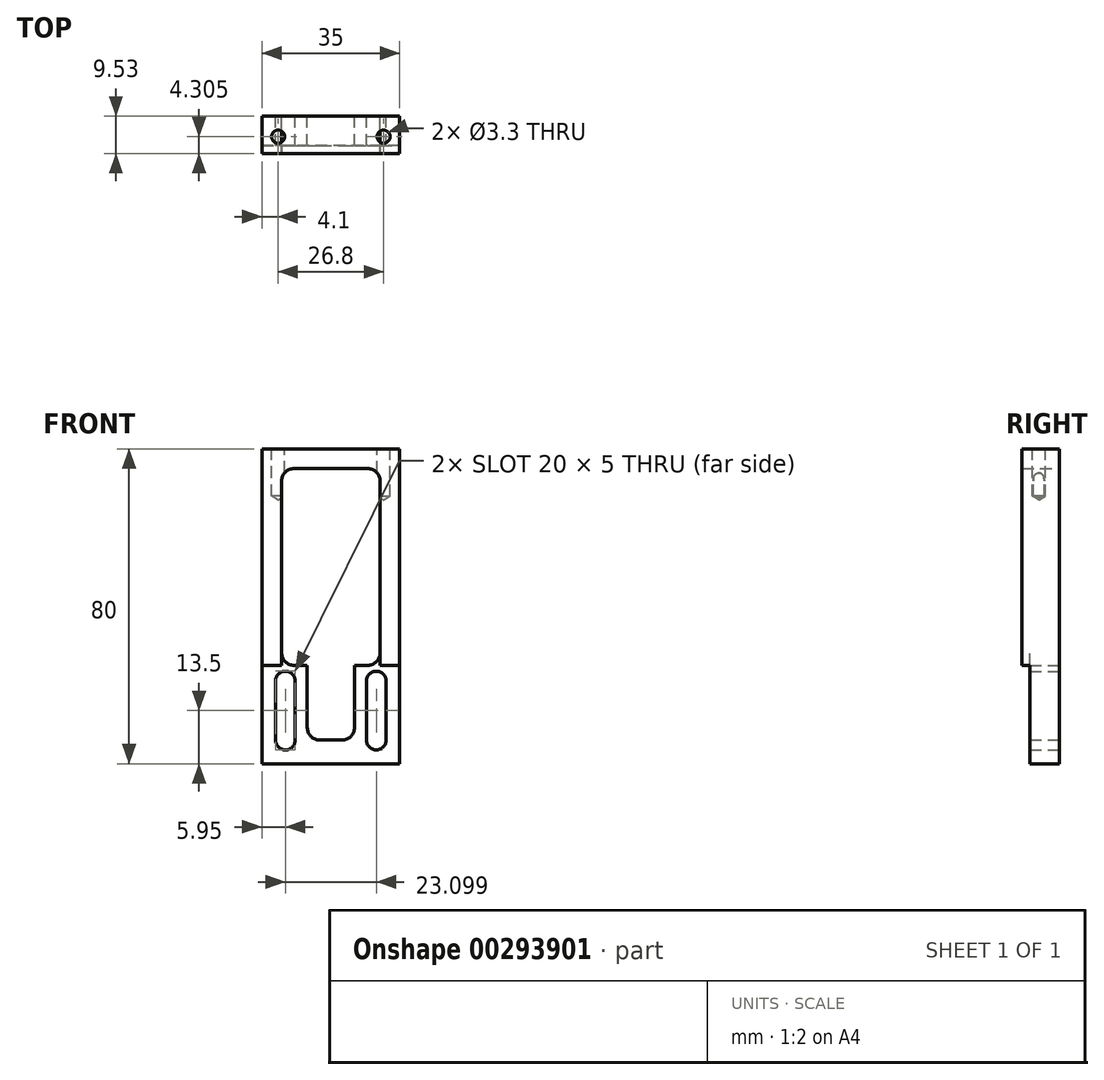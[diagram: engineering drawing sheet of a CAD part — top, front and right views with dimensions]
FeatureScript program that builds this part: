
annotation { "Feature Type Name" : "Feature", "Feature Type Description" : "" }
export const myFeature = defineFeature(function(context is Context, id is Id, definition is map)
    precondition{}
    {
        {
            var Q0;
            Q0=qCreatedBy(makeId("Front.planeOp"),FACE);
            var sketch = newSketch(context, id + "F0", { "sketchPlane" : qUnion([Q0])});
            skLineSegment(sketch, "E0.bottom", {"start": v(17.5, -40) * mm, "end": v(-17.5, -40) * mm});
            skLineSegment(sketch, "E0.top", {"start": v(17.5, 40) * mm, "end": v(-17.5, 40) * mm});
            skLineSegment(sketch, "E0.left", {"start": v(17.5, -40) * mm, "end": v(17.5, 40) * mm});
            skLineSegment(sketch, "E0.right", {"start": v(-17.5, -40) * mm, "end": v(-17.5, 40) * mm});
            skPoint(sketch, "E0.middle", {"position": v(0, 0) * mm});
            skLineSegment(sketch, "E1", {"start": v(-17.5, -15) * mm, "end": v(17.5, -15) * mm});
            skLineSegment(sketch, "E2.bottom", {"start": v(-9.33, 35) * mm, "end": v(9.32, 35) * mm});
            skLineSegment(sketch, "E2.top", {"start": v(-9.32, -15) * mm, "end": v(9.32, -15) * mm});
            skLineSegment(sketch, "E2.left", {"start": v(-12.5, 31.83) * mm, "end": v(-12.5, -11.82) * mm});
            skLineSegment(sketch, "E2.right", {"start": v(12.5, 31.83) * mm, "end": v(12.5, -11.82) * mm});
            skLineSegment(sketch, "E3.bottom", {"start": v(-6, -15) * mm, "end": v(6, -15) * mm});
            skLineSegment(sketch, "E3.top", {"start": v(-2.82, -34) * mm, "end": v(2.83, -34) * mm});
            skLineSegment(sketch, "E3.left", {"start": v(-6, -15) * mm, "end": v(-6, -30.83) * mm});
            skLineSegment(sketch, "E3.right", {"start": v(6, -15) * mm, "end": v(6, -30.83) * mm});
            skPoint(sketch, "E4.visualSharp", {"position": v(-12.5, 35) * mm});
            skArc(sketch, "E4.filletArc", {"start": v(-9.33, 35) * mm, "mid": v(-11.57, 34.07) * mm, "end": v(-12.5, 31.83) * mm});
            skPoint(sketch, "E5.visualSharp", {"position": v(12.5, 35) * mm});
            skArc(sketch, "E5.filletArc", {"start": v(12.5, 31.83) * mm, "mid": v(11.57, 34.07) * mm, "end": v(9.32, 35) * mm});
            skPoint(sketch, "E6.visualSharp", {"position": v(-12.5, -15) * mm});
            skArc(sketch, "E6.filletArc", {"start": v(-12.5, -11.82) * mm, "mid": v(-11.57, -14.07) * mm, "end": v(-9.32, -15) * mm});
            skPoint(sketch, "E7.visualSharp", {"position": v(12.5, -15) * mm});
            skArc(sketch, "E7.filletArc", {"start": v(9.32, -15) * mm, "mid": v(11.57, -14.07) * mm, "end": v(12.5, -11.82) * mm});
            skPoint(sketch, "E8.visualSharp", {"position": v(-6, -34) * mm});
            skArc(sketch, "E8.filletArc", {"start": v(-6, -30.83) * mm, "mid": v(-5.07, -33.07) * mm, "end": v(-2.82, -34) * mm});
            skPoint(sketch, "E9.visualSharp", {"position": v(6, -34) * mm});
            skArc(sketch, "E9.filletArc", {"start": v(2.83, -34) * mm, "mid": v(5.07, -33.07) * mm, "end": v(6, -30.83) * mm});
            skLineSegment(sketch, "E10.bottom", {"start": v(-11.55, -36.5) * mm, "end": v(-11.55, -36.5) * mm});
            skLineSegment(sketch, "E10.top", {"start": v(-11.55, -16.5) * mm, "end": v(-11.55, -16.5) * mm});
            skLineSegment(sketch, "E10.left", {"start": v(-9.05, -34) * mm, "end": v(-9.05, -19) * mm});
            skLineSegment(sketch, "E10.right", {"start": v(-14.05, -34) * mm, "end": v(-14.05, -19) * mm});
            skPoint(sketch, "E10.middle", {"position": v(-11.55, -26.5) * mm});
            skPoint(sketch, "E11.visualSharp", {"position": v(-14.05, -16.5) * mm});
            skArc(sketch, "E11.filletArc", {"start": v(-11.55, -16.5) * mm, "mid": v(-13.32, -17.23) * mm, "end": v(-14.05, -19) * mm});
            skPoint(sketch, "E12.visualSharp", {"position": v(-9.05, -16.5) * mm});
            skArc(sketch, "E12.filletArc", {"start": v(-9.05, -19) * mm, "mid": v(-9.78, -17.23) * mm, "end": v(-11.55, -16.5) * mm});
            skPoint(sketch, "E13.visualSharp", {"position": v(-14.05, -36.5) * mm});
            skArc(sketch, "E13.filletArc", {"start": v(-14.05, -34) * mm, "mid": v(-13.32, -35.77) * mm, "end": v(-11.55, -36.5) * mm});
            skPoint(sketch, "E14.visualSharp", {"position": v(-9.05, -36.5) * mm});
            skArc(sketch, "E14.filletArc", {"start": v(-11.55, -36.5) * mm, "mid": v(-9.78, -35.77) * mm, "end": v(-9.05, -34) * mm});
            skLineSegment(sketch, "E15.MirrorCS", {"start": v(11.55, -16.5) * mm, "end": v(11.55, -16.5) * mm});
            skPoint(sketch, "E16.MirrorP", {"position": v(14.05, -16.5) * mm});
            skLineSegment(sketch, "E17.MirrorCS", {"start": v(9.05, -34) * mm, "end": v(9.05, -19) * mm});
            skArc(sketch, "E18.MirrorCS", {"start": v(14.05, -34) * mm, "mid": v(13.32, -35.77) * mm, "end": v(11.55, -36.5) * mm});
            skPoint(sketch, "E19.MirrorP", {"position": v(9.05, -16.5) * mm});
            skArc(sketch, "E20.MirrorCS", {"start": v(9.05, -19) * mm, "mid": v(9.78, -17.23) * mm, "end": v(11.55, -16.5) * mm});
            skPoint(sketch, "E21.MirrorP", {"position": v(11.55, -26.5) * mm});
            skPoint(sketch, "E22.MirrorP", {"position": v(14.05, -36.5) * mm});
            skLineSegment(sketch, "E23.MirrorCS", {"start": v(11.55, -36.5) * mm, "end": v(11.55, -36.5) * mm});
            skLineSegment(sketch, "E24.MirrorCS", {"start": v(14.05, -34) * mm, "end": v(14.05, -19) * mm});
            skArc(sketch, "E25.MirrorCS", {"start": v(11.55, -16.5) * mm, "mid": v(13.32, -17.23) * mm, "end": v(14.05, -19) * mm});
            skArc(sketch, "E26.MirrorCS", {"start": v(11.55, -36.5) * mm, "mid": v(9.78, -35.77) * mm, "end": v(9.05, -34) * mm});
            skPoint(sketch, "E27.MirrorP", {"position": v(9.05, -36.5) * mm});
            skSolve(sketch);
        }
        {
            var Q0;
            Q0 = qSketchRegion(id + "F0", true);
            extrude(context, id + "F1", {"entities" : qUnion([Q0]), "depth" : 9.52 * mm});
        }
        {
            var Q0;
            Q0=makeQuery(id+"F1.opExtrude","CAP_FACE",FACE,{"disambiguationData":[OSD([sQuery(id+"F0.wireOp",EDGE,"E0.bottom"),sQuery(id+"F0.wireOp",EDGE,"E0.top"),sQuery(id+"F0.wireOp",EDGE,"E0.left"),sQuery(id+"F0.wireOp",EDGE,"E0.right"),sQuery(id+"F0.wireOp",EDGE,"E2.bottom"),sQuery(id+"F0.wireOp",EDGE,"E2.top"),sQuery(id+"F0.wireOp",EDGE,"E2.left"),sQuery(id+"F0.wireOp",EDGE,"E2.right"),sQuery(id+"F0.wireOp",EDGE,"E3.top"),sQuery(id+"F0.wireOp",EDGE,"E3.left"),sQuery(id+"F0.wireOp",EDGE,"E3.right"),sQuery(id+"F0.wireOp",EDGE,"E4.filletArc"),sQuery(id+"F0.wireOp",EDGE,"E5.filletArc"),sQuery(id+"F0.wireOp",EDGE,"E6.filletArc"),sQuery(id+"F0.wireOp",EDGE,"E7.filletArc"),sQuery(id+"F0.wireOp",EDGE,"E8.filletArc"),sQuery(id+"F0.wireOp",EDGE,"E9.filletArc"),sQuery(id+"F0.wireOp",EDGE,"E10.left"),sQuery(id+"F0.wireOp",EDGE,"E10.right"),sQuery(id+"F0.wireOp",EDGE,"E11.filletArc"),sQuery(id+"F0.wireOp",EDGE,"E12.filletArc"),sQuery(id+"F0.wireOp",EDGE,"E13.filletArc"),sQuery(id+"F0.wireOp",EDGE,"E14.filletArc"),sQuery(id+"F0.wireOp",EDGE,"E17.MirrorCS"),sQuery(id+"F0.wireOp",EDGE,"E18.MirrorCS"),sQuery(id+"F0.wireOp",EDGE,"E20.MirrorCS"),sQuery(id+"F0.wireOp",EDGE,"E24.MirrorCS"),sQuery(id+"F0.wireOp",EDGE,"E25.MirrorCS"),sQuery(id+"F0.wireOp",EDGE,"E26.MirrorCS")])],"isStart":false});
            var sketch = newSketch(context, id + "F2", { "sketchPlane" : qUnion([Q0])});
            skLineSegment(sketch, "E28", {"start": v(-17.5, -15) * mm, "end": v(17.5, -15) * mm});
            skSolve(sketch);
        }
        {
            var Q0;
            {var subQ0=makeQuery(id+"F1.opExtrude","CAP_EDGE",EDGE,{"disambiguationData":[OSD([sQuery(id+"F0.wireOp",EDGE,"E0.bottom")])],"isStart":false});Q0=makeQuery(id+"F2.imprint","IMPRINT",FACE,{"disambiguationData":[TD([[makeQuery(id+"F2.imprint","IMPRINT",EDGE,{"derivedFrom":subQ0}),-1.0]])]});}
            extrude(context, id + "F3", {"entities" : qUnion([Q0]), "operationType" : NewBodyOperationType.REMOVE, "oppositeDirection" : true, "depth" : 2 * mm});
        }
        {
            var Q0;
            Q0=makeQuery(id+"F1.opExtrude","SWEPT_FACE",FACE,{"disambiguationData":[OSD([sQuery(id+"F0.wireOp",EDGE,"E0.top")])]});
            var sketch = newSketch(context, id + "F4", { "sketchPlane" : qUnion([Q0])});
            skPoint(sketch, "E29", {"position": v(-13.4, -5.23) * mm});
            skPoint(sketch, "E30", {"position": v(13.4, -5.23) * mm});
            skSolve(sketch);
        }
        {
            var Q0;
            Q0=sQuery(id+"F4.wireOp",VERTEX,"E29");
            var Q1;
            Q1=sQuery(id+"F4.wireOp",VERTEX,"E30");
            var Q2;
            Q2=makeQuery(id+"F1.opExtrude","SWEPT_BODY",BODY,{"disambiguationData":[OSD([sQuery(id+"F0.wireOp",EDGE,"E0.bottom"),sQuery(id+"F0.wireOp",EDGE,"E0.top"),sQuery(id+"F0.wireOp",EDGE,"E0.left"),sQuery(id+"F0.wireOp",EDGE,"E0.right"),sQuery(id+"F0.wireOp",EDGE,"E2.bottom"),sQuery(id+"F0.wireOp",EDGE,"E2.top"),sQuery(id+"F0.wireOp",EDGE,"E2.left"),sQuery(id+"F0.wireOp",EDGE,"E2.right"),sQuery(id+"F0.wireOp",EDGE,"E3.top"),sQuery(id+"F0.wireOp",EDGE,"E3.left"),sQuery(id+"F0.wireOp",EDGE,"E3.right"),sQuery(id+"F0.wireOp",EDGE,"E4.filletArc"),sQuery(id+"F0.wireOp",EDGE,"E5.filletArc"),sQuery(id+"F0.wireOp",EDGE,"E6.filletArc"),sQuery(id+"F0.wireOp",EDGE,"E7.filletArc"),sQuery(id+"F0.wireOp",EDGE,"E8.filletArc"),sQuery(id+"F0.wireOp",EDGE,"E9.filletArc"),sQuery(id+"F0.wireOp",EDGE,"E10.left"),sQuery(id+"F0.wireOp",EDGE,"E10.right"),sQuery(id+"F0.wireOp",EDGE,"E11.filletArc"),sQuery(id+"F0.wireOp",EDGE,"E12.filletArc"),sQuery(id+"F0.wireOp",EDGE,"E13.filletArc"),sQuery(id+"F0.wireOp",EDGE,"E14.filletArc"),sQuery(id+"F0.wireOp",EDGE,"E17.MirrorCS"),sQuery(id+"F0.wireOp",EDGE,"E18.MirrorCS"),sQuery(id+"F0.wireOp",EDGE,"E20.MirrorCS"),sQuery(id+"F0.wireOp",EDGE,"E24.MirrorCS"),sQuery(id+"F0.wireOp",EDGE,"E25.MirrorCS"),sQuery(id+"F0.wireOp",EDGE,"E26.MirrorCS")])]});
            hole(context, id + "F5", {"style" : HoleStyle.SIMPLE, "endStyle" : HoleEndStyle.BLIND, "standardTappedOrClearance" : lookupTablePath({ "standard" : "ISO", "fit" : "Normal", "size" : "M3", "type" : "Clearance" }), "standardBlindInLast" : lookupTablePath({ "fit" : "Standard", "standard" : "ISO", "size" : "M3", "type" : "Clearance" }), "holeDiameter" : 3.3 * mm, "holeDepth" : 12 * mm, "tappedDepth" : 12 * mm, "tapClearance" : 3, "startFromSketch" : true, "locations" : qUnion([Q0, Q1]), "scope" : qUnion([Q2])});
        }
        {
            var Q0;
            Q0=makeQuery(id+"F1.opExtrude","CAP_FACE",FACE,{"disambiguationData":[OSD([sQuery(id+"F0.wireOp",EDGE,"E0.bottom"),sQuery(id+"F0.wireOp",EDGE,"E0.top"),sQuery(id+"F0.wireOp",EDGE,"E0.left"),sQuery(id+"F0.wireOp",EDGE,"E0.right"),sQuery(id+"F0.wireOp",EDGE,"E2.bottom"),sQuery(id+"F0.wireOp",EDGE,"E2.top"),sQuery(id+"F0.wireOp",EDGE,"E2.left"),sQuery(id+"F0.wireOp",EDGE,"E2.right"),sQuery(id+"F0.wireOp",EDGE,"E3.top"),sQuery(id+"F0.wireOp",EDGE,"E3.left"),sQuery(id+"F0.wireOp",EDGE,"E3.right"),sQuery(id+"F0.wireOp",EDGE,"E4.filletArc"),sQuery(id+"F0.wireOp",EDGE,"E5.filletArc"),sQuery(id+"F0.wireOp",EDGE,"E6.filletArc"),sQuery(id+"F0.wireOp",EDGE,"E7.filletArc"),sQuery(id+"F0.wireOp",EDGE,"E8.filletArc"),sQuery(id+"F0.wireOp",EDGE,"E9.filletArc"),sQuery(id+"F0.wireOp",EDGE,"E10.left"),sQuery(id+"F0.wireOp",EDGE,"E10.right"),sQuery(id+"F0.wireOp",EDGE,"E11.filletArc"),sQuery(id+"F0.wireOp",EDGE,"E12.filletArc"),sQuery(id+"F0.wireOp",EDGE,"E13.filletArc"),sQuery(id+"F0.wireOp",EDGE,"E14.filletArc"),sQuery(id+"F0.wireOp",EDGE,"E17.MirrorCS"),sQuery(id+"F0.wireOp",EDGE,"E18.MirrorCS"),sQuery(id+"F0.wireOp",EDGE,"E20.MirrorCS"),sQuery(id+"F0.wireOp",EDGE,"E24.MirrorCS"),sQuery(id+"F0.wireOp",EDGE,"E25.MirrorCS"),sQuery(id+"F0.wireOp",EDGE,"E26.MirrorCS")])],"isStart":false});
            var sketch = newSketch(context, id + "F6", { "sketchPlane" : qUnion([Q0])});
            skLineSegment(sketch, "E31", {"start": v(-12.5, -11.82) * mm, "end": v(-12.5, -15) * mm});
            skLineSegment(sketch, "E32", {"start": v(-12.5, -15) * mm, "end": v(-9.33, -15) * mm});
            skLineSegment(sketch, "E33", {"start": v(12.5, -11.82) * mm, "end": v(12.5, -15) * mm});
            skLineSegment(sketch, "E34", {"start": v(12.5, -15) * mm, "end": v(9.33, -15) * mm});
            skSolve(sketch);
        }
        {
            var Q0;
            Q0=makeQuery(id+"F6.imprint","IMPRINT",FACE,{"disambiguationData":[TD([[makeQuery(id+"F6.imprint","IMPRINT",EDGE,{"derivedFrom":sQuery(id+"F6.wireOp",EDGE,"E31")}),1.0]])]});
            var Q1;
            Q1=makeQuery(id+"F6.imprint","IMPRINT",FACE,{"disambiguationData":[TD([[makeQuery(id+"F6.imprint","IMPRINT",EDGE,{"derivedFrom":sQuery(id+"F6.wireOp",EDGE,"E33")}),-1.0]])]});
            var Q2;
            Q2=makeQuery(id+"F3.boolean.opBoolean","COPY",FACE,{"derivedFrom":makeQuery(id+"F3.opExtrude","CAP_FACE",FACE,{"disambiguationData":[OSD([sQuery(id+"F0.wireOp",EDGE,"E0.bottom"),sQuery(id+"F0.wireOp",EDGE,"E0.left"),sQuery(id+"F0.wireOp",EDGE,"E0.right"),sQuery(id+"F0.wireOp",EDGE,"E3.top"),sQuery(id+"F0.wireOp",EDGE,"E3.left"),sQuery(id+"F0.wireOp",EDGE,"E3.right"),sQuery(id+"F0.wireOp",EDGE,"E8.filletArc"),sQuery(id+"F0.wireOp",EDGE,"E9.filletArc"),sQuery(id+"F0.wireOp",EDGE,"E10.left"),sQuery(id+"F0.wireOp",EDGE,"E10.right"),sQuery(id+"F0.wireOp",EDGE,"E11.filletArc"),sQuery(id+"F0.wireOp",EDGE,"E12.filletArc"),sQuery(id+"F0.wireOp",EDGE,"E13.filletArc"),sQuery(id+"F0.wireOp",EDGE,"E14.filletArc"),sQuery(id+"F0.wireOp",EDGE,"E17.MirrorCS"),sQuery(id+"F0.wireOp",EDGE,"E18.MirrorCS"),sQuery(id+"F0.wireOp",EDGE,"E20.MirrorCS"),sQuery(id+"F0.wireOp",EDGE,"E24.MirrorCS"),sQuery(id+"F0.wireOp",EDGE,"E25.MirrorCS"),sQuery(id+"F0.wireOp",EDGE,"E26.MirrorCS"),sQuery(id+"F2.wireOp",EDGE,"E28")])],"isStart":false})});
            extrude(context, id + "F7", {"entities" : qUnion([Q0, Q1]), "operationType" : NewBodyOperationType.REMOVE, "endBound" : BoundingType.UP_TO_SURFACE, "oppositeDirection" : true, "endBoundEntityFace" : qUnion([Q2]), "depth" : 25 * mm});
        }
    });
